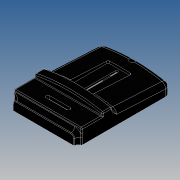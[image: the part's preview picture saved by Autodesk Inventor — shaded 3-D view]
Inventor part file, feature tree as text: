
AUTODESK INVENTOR PART (.ipt)
format: ipt  version: 2016 (Build 200138000, 138)  size: 879,104 bytes
history: native  units: mm
features: sketch x20, extrude x19, fillet x7, plane x4, direct_edit x2, hole x2, projected_geometry x2, move_body x2, shell x1, chamfer x1
ambient origin geometry x8: Origin, YZ Plane, XZ Plane, XY Plane, X Axis, Y Axis, Z Axis, Center Point
bodies: Solid1 (feature_tree)
feature tree (60):
  extrude  "Extrusion1"  Depth=150.0mm
  plane  "Work Plane2"
  extrude  "Extrusion2"  Depth=36.0mm
  sketch  "Sketch3"  dims[d9=30.0mm d10=16.5mm d11=0.0mm d13=-35.0mm d14=7.0mm]
  direct_edit  "Direct Edit1"
  extrude  "Extrusion3"  Depth=16.5mm TaperAngle=0.0deg
  fillet  "Fillet1"  [1 undecoded]
  fillet  "Fillet2"  Radius=7.0mm
  fillet  "Fillet3"  Radius=104.75mm
  plane  "Work Plane7"
  extrude  "Extrusion19"  Depth=2.0mm
  shell  "Shell1"  Thickness=1.0mm
  extrude  "Extrusion4"  Depth=104.0mm
  fillet  "Fillet4"  Radius=16.0mm
  fillet  "Fillet5"  Radius=7.0mm
  fillet  "Fillet6"  Radius=6.0mm
  direct_edit  "Direct Edit2"
  sketch  "Sketch17"  dims[d84=8.0mm d85=10.0mm]
  extrude  "Extrusion17"  Depth=1.0mm
  extrude  "Extrusion18"  Depth=2.0mm
  extrude  "Extrusion11"  Depth=2.0mm
  extrude  "Extrusion12"  Depth=6.0mm
  extrude  "Extrusion13"  Depth=10.0mm
  extrude  "Extrusion14"  Depth=12.8mm
  extrude  "Extrusion15"  Depth=1.5mm TaperAngle=0.0deg
  plane  "Work Plane3"
  extrude  "Extrusion16"  Depth=1.8mm TaperAngle=0.0deg
  extrude  "Extrusion20"  Depth=3.5mm
  extrude  "Extrusion21"  Depth=9.0mm
  extrude  "Extrusion22"  Depth=2.5mm
  extrude  "Extrusion23"  Depth=10.0mm
  fillet  "Fillet9"  Radius=10.0mm
  plane  "Work Plane8"
  extrude  "Extrusion24"  Depth=14.0mm
  extrude  "Extrusion25"  Depth=10.0mm
  hole  "Hole2"  [1 undecoded]
  hole  "Hole3"  [1 undecoded]
  chamfer  "Chamfer2"  Distance=3.0mm
  sketch  "Sketch1"  dims[d0=115.0mm d1=150.0mm]
  sketch  "Sketch2"  dims[d2=25.0mm d3=0.0mm d8=36.0mm]
  sketch  "Sketch4"  dims[d15=0.0mm d16=0.0mm d17=5.0mm d18=104.75mm d19=0.523599mm]
  sketch  "Sketch11"  dims[d20=8.0mm d21=2.0mm d22=1.0mm]
  sketch  "Sketch12"  dims[d23=3.0mm d24=104.0mm d25=16.0mm d26=7.0mm d27=0.0mm d28=6.0mm]
  sketch  "Sketch13"  dims[d29=1.5mm d30=1.0mm]
  sketch  "Sketch14"  dims[d43=0.0mm d44=0.0mm d45=6.0mm d79=2.0mm]
  sketch  "Sketch15"  dims[d80=1.0mm d81=2.0mm]
  projected_geometry  "Projected Loop1"
  sketch  "Sketch16"  dims[d82=1.0mm d83=6.0mm]
  sketch  "Sketch18"  dims[d86=1.5mm d87=0.0mm d88=12.8mm]
  sketch  "Sketch19"  dims[d89=14.5mm d90=1.5mm d91=0.0mm]
  projected_geometry  "Projected Loop2"
  sketch  "Sketch20"  dims[d92=3.0mm d93=1.8mm d94=0.0mm]
  sketch  "Sketch21"  dims[d95=68.0mm d96=3.5mm]
  sketch  "Sketch22"  dims[d97=1.8mm d98=0.0mm d99=9.0mm]
  sketch  "Sketch23"  dims[d100=1.8mm d101=0.0mm d102=2.5mm]
  sketch  "Sketch24"  dims[d103=10.0mm d104=10.0mm d105=10.0mm]
  sketch  "Sketch25"  dims[d106=2.8mm d107=14.0mm]
  sketch  "Sketch26"  dims[d108=32.0mm d109=45.0mm d110=1.8mm d111=0.0mm d113=3.0mm d114=3.0mm d115=3.0mm d116=3.0mm d117=3.0mm d118=3.0mm d119=55.5mm d120=3.0mm d121=27.5mm d122=1.0mm d123=14.0mm d124=0.0mm d125=10.0mm d126=0.0mm d127=1.0mm d128=40.0mm d129=70.6mm d130=2.0mm d131=13.5mm d132=0.0mm d133=4.5mm d134=60.0mm d135=13.5mm d136=0.0mm d137=35.0mm d138=3.0mm d139=13.5mm d140=0.0mm d141=60.0mm d142=2.5mm d143=0.0mm d144=4.0mm d145=44.0mm d146=4.0mm d147=9.0mm d148=2.5mm d149=0.0mm d150=2.0mm d151=12.5mm d152=8.8mm d153=26.5mm d154=34.0mm d155=42.0mm d156=31.0mm d157=8.0mm d158=4.0mm d159=6.0mm d160=0.0mm d161=0.349066mm d162=22.7mm d163=8.5mm d164=14.5mm d165=2.5mm d166=0.349066mm d167=2.459mm d168=6.0mm d169=4.0mm d170=2.0mm d171=90.0deg d172=8.8mm d173=20.594885mm d174=2.459mm d175=6.0mm d176=4.0mm d177=2.0mm d178=90.0deg d179=8.8mm d180=20.594885mm d181=1.0mm d182=2.0mm d183=45.0deg]
  move_body  "Move1"
  move_body  "Move2"
note: 3 required parameter values undecoded (feature->parameter linkage not recoverable at this tier; creation-order binding heuristic only, values carry confidence <= 0.55)
